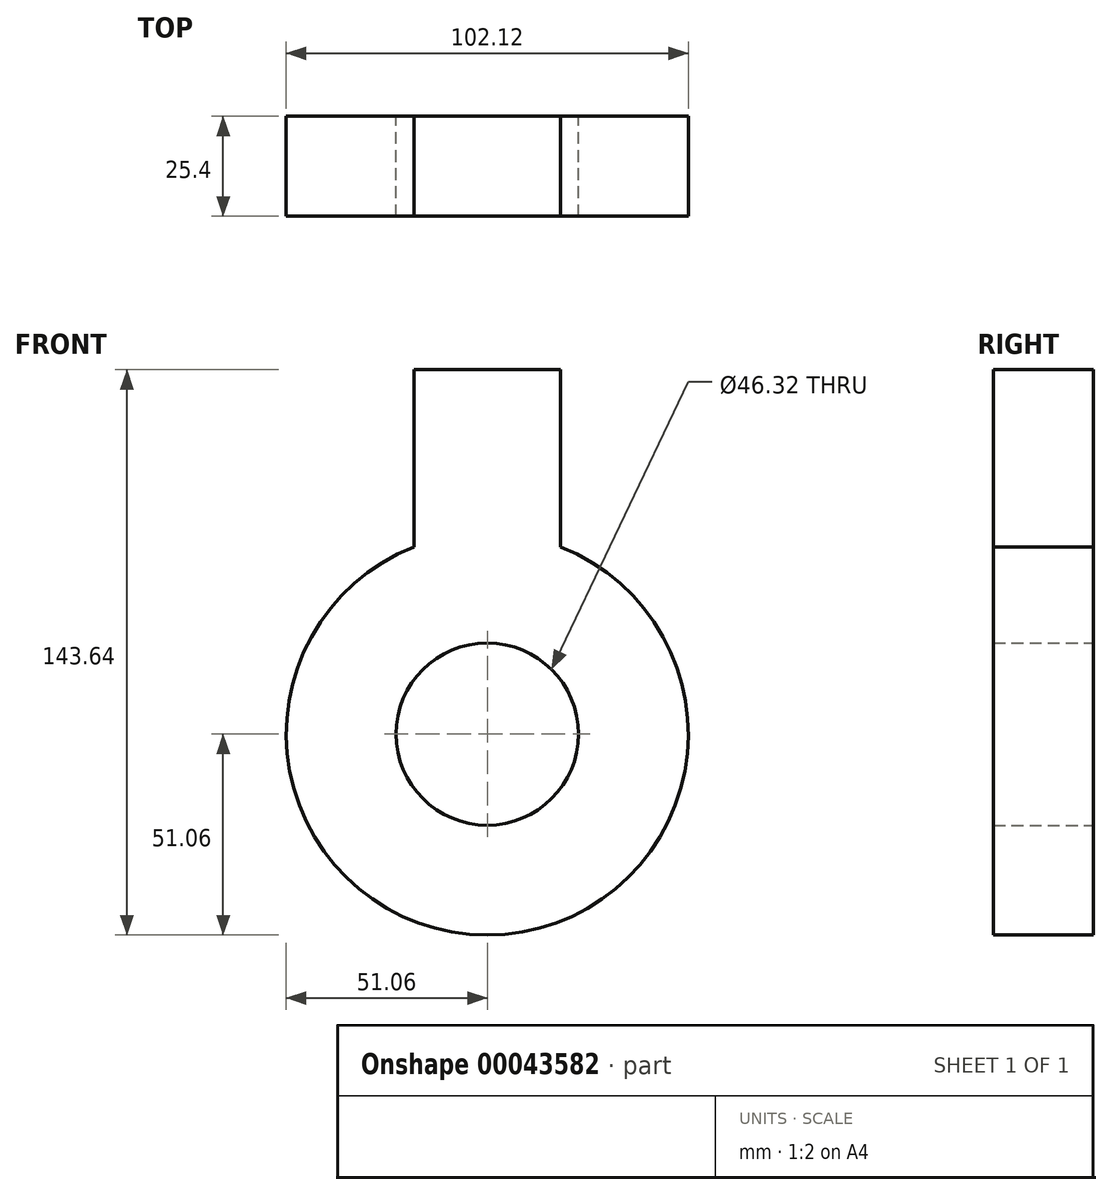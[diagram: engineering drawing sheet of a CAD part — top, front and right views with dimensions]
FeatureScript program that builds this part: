
annotation { "Feature Type Name" : "Feature", "Feature Type Description" : "" }
export const myFeature = defineFeature(function(context is Context, id is Id, definition is map)
    precondition{}
    {
        {
            var Q0;
            Q0=qCreatedBy(makeId("Front.planeOp"),FACE);
            var sketch = newSketch(context, id + "F0", { "sketchPlane" : qUnion([Q0])});
            skCircle(sketch, "E0", {"center": v(0, 0) * mm, "radius": 23.16 * mm});
            skCircle(sketch, "E1", {"center": v(0, 0) * mm, "radius": 51.06 * mm});
            skLineSegment(sketch, "E2.bottom", {"start": v(-18.6, 40.7) * mm, "end": v(18.6, 40.7) * mm});
            skLineSegment(sketch, "E2.top", {"start": v(-18.6, 92.58) * mm, "end": v(18.6, 92.58) * mm});
            skLineSegment(sketch, "E2.left", {"start": v(-18.6, 40.7) * mm, "end": v(-18.6, 92.58) * mm});
            skLineSegment(sketch, "E2.right", {"start": v(18.6, 40.7) * mm, "end": v(18.6, 92.58) * mm});
            skLineSegment(sketch, "E3", {"start": v(0, 40.7) * mm, "end": v(0, 0) * mm, "construction": true});
            skSolve(sketch);
        }
        {
            var Q0;
            Q0 = qSketchRegion(id + "F0", true);
            extrude(context, id + "F1", {"entities" : qUnion([Q0]), "depth" : 25.4 * mm});
        }
    });
